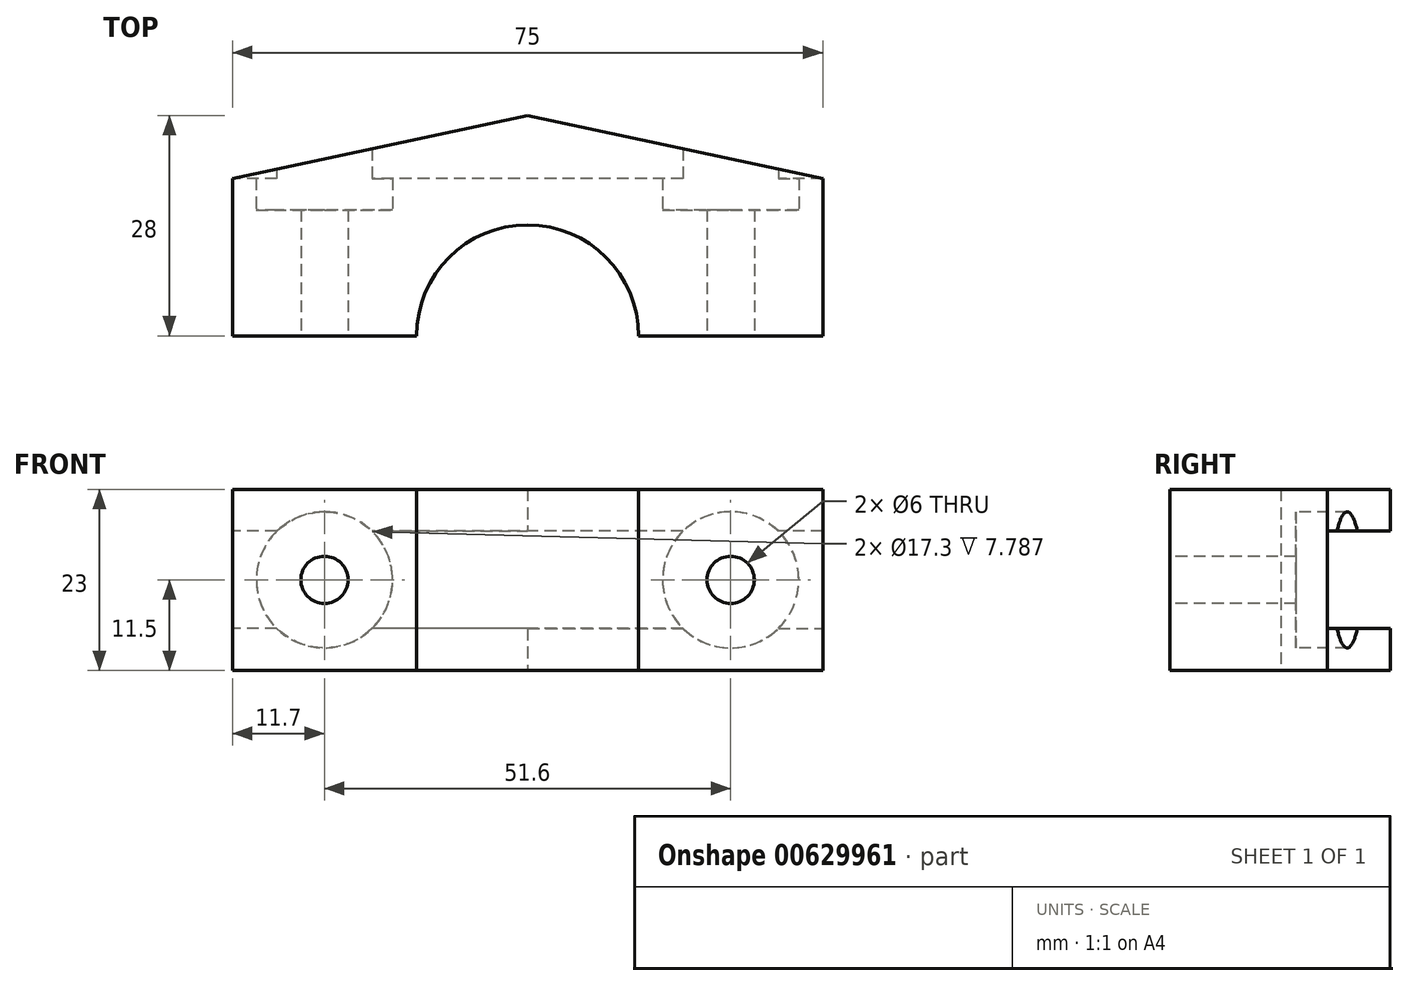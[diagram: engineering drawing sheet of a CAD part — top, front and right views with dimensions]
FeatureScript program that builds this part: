
annotation { "Feature Type Name" : "Feature", "Feature Type Description" : "" }
export const myFeature = defineFeature(function(context is Context, id is Id, definition is map)
    precondition{}
    {
        {
            var Q0;
            Q0=qCreatedBy(makeId("Top.planeOp"),FACE);
            var sketch = newSketch(context, id + "F0", { "sketchPlane" : qUnion([Q0])});
            skLineSegment(sketch, "E0.bottom", {"start": v(-37.5, 20) * mm, "end": v(37.5, 20) * mm});
            skLineSegment(sketch, "E0.top", {"start": v(-37.5, 0) * mm, "end": v(-14.1, 0) * mm});
            skLineSegment(sketch, "E0.left", {"start": v(-37.5, 20) * mm, "end": v(-37.5, 0) * mm});
            skLineSegment(sketch, "E0.right", {"start": v(37.5, 20) * mm, "end": v(37.5, 0) * mm});
            skLineSegment(sketch, "E1", {"start": v(14.1, 0) * mm, "end": v(37.5, 0) * mm});
            skArc(sketch, "E2", {"start": v(14.1, 0) * mm, "mid": v(0, 14.1) * mm, "end": v(-14.1, 0) * mm});
            skSolve(sketch);
        }
        {
            var Q0;
            Q0=makeQuery(id+"F0.imprint","IMPRINT",FACE,{"disambiguationData":[TD([[makeQuery(id+"F0.imprint","IMPRINT",EDGE,{"derivedFrom":sQuery(id+"F0.wireOp",EDGE,"E0.bottom")}),-1.0]])]});
            extrude(context, id + "F1", {"entities" : qUnion([Q0]), "depth" : 23 * mm, "offsetDistance" : 25 * mm});
        }
        {
            var Q0;
            Q0=makeQuery(id+"F1.opExtrude","SWEPT_FACE",FACE,{"disambiguationData":[OSD([sQuery(id+"F0.wireOp",EDGE,"E0.top")])]});
            var sketch = newSketch(context, id + "F2", { "sketchPlane" : qUnion([Q0])});
            skLineSegment(sketch, "E3", {"start": v(-14.1, 23) * mm, "end": v(-25.8, 11.5) * mm});
            skLineSegment(sketch, "E4", {"start": v(-37.5, 0) * mm, "end": v(-37.5, 23) * mm});
            skLineSegment(sketch, "E5", {"start": v(-37.5, 23) * mm, "end": v(-14.1, 0) * mm});
            skLineSegment(sketch, "E6", {"start": v(-25.8, 11.5) * mm, "end": v(-37.5, 0) * mm});
            skCircle(sketch, "E7", {"center": v(-25.8, 11.5) * mm, "radius": 3.02 * mm});
            skSolve(sketch);
        }
        {
            var Q0;
            Q0=makeQuery(id+"F1.opExtrude","SWEPT_FACE",FACE,{"disambiguationData":[OSD([sQuery(id+"F0.wireOp",EDGE,"E1")])]});
            var sketch = newSketch(context, id + "F3", { "sketchPlane" : qUnion([Q0])});
            skLineSegment(sketch, "E8", {"start": v(14.1, 23) * mm, "end": v(37.5, 0) * mm});
            skLineSegment(sketch, "E9", {"start": v(37.5, 0) * mm, "end": v(37.5, 23) * mm});
            skLineSegment(sketch, "E10", {"start": v(37.5, 23) * mm, "end": v(14.1, 0) * mm});
            skCircle(sketch, "E11", {"center": v(25.8, 11.5) * mm, "radius": 3 * mm});
            skSolve(sketch);
        }
        {
            var Q0;
            Q0=sQuery(id+"F2.wireOp",VERTEX,"E7.center");
            var Q1;
            Q1=makeQuery(id+"F1.opExtrude","SWEPT_BODY",BODY,{"disambiguationData":[OSD([sQuery(id+"F0.wireOp",EDGE,"E0.bottom"),sQuery(id+"F0.wireOp",EDGE,"E0.top"),sQuery(id+"F0.wireOp",EDGE,"E0.left"),sQuery(id+"F0.wireOp",EDGE,"E0.right"),sQuery(id+"F0.wireOp",EDGE,"E1"),sQuery(id+"F0.wireOp",EDGE,"E2")])]});
            hole(context, id + "F4", {"style" : HoleStyle.SIMPLE, "endStyle" : HoleEndStyle.THROUGH, "holeDiameter" : 6 * mm, "majorDiameter" : 5 * mm, "isTappedThrough" : true, "tappedDepth" : 12 * mm, "tapClearance" : 3, "locations" : qUnion([Q0]), "scope" : qUnion([Q1])});
        }
        {
            var Q0;
            Q0=sQuery(id+"F3.wireOp",VERTEX,"E11.center");
            var Q1;
            Q1=makeQuery(id+"F1.opExtrude","SWEPT_BODY",BODY,{"disambiguationData":[OSD([sQuery(id+"F0.wireOp",EDGE,"E0.bottom"),sQuery(id+"F0.wireOp",EDGE,"E0.top"),sQuery(id+"F0.wireOp",EDGE,"E0.left"),sQuery(id+"F0.wireOp",EDGE,"E0.right"),sQuery(id+"F0.wireOp",EDGE,"E1"),sQuery(id+"F0.wireOp",EDGE,"E2")])]});
            hole(context, id + "F5", {"style" : HoleStyle.SIMPLE, "endStyle" : HoleEndStyle.THROUGH, "holeDiameter" : 6 * mm, "majorDiameter" : 5 * mm, "isTappedThrough" : true, "tappedDepth" : 12 * mm, "tapClearance" : 3, "locations" : qUnion([Q0]), "scope" : qUnion([Q1])});
        }
        {
            var Q0;
            Q0=makeQuery(id+"F1.opExtrude","SWEPT_FACE",FACE,{"disambiguationData":[OSD([sQuery(id+"F0.wireOp",EDGE,"E0.bottom")])]});
            var sketch = newSketch(context, id + "F6", { "sketchPlane" : qUnion([Q0])});
            skLineSegment(sketch, "E12.bottom", {"start": v(-37.5, 23) * mm, "end": v(37.5, 23) * mm});
            skLineSegment(sketch, "E12.top", {"start": v(-37.5, 17.68) * mm, "end": v(-37.5, 17.68) * mm});
            skLineSegment(sketch, "E12.left", {"start": v(-37.5, 23) * mm, "end": v(-37.5, 17.68) * mm});
            skLineSegment(sketch, "E12.right", {"start": v(37.5, 23) * mm, "end": v(37.5, 17.68) * mm});
            skLineSegment(sketch, "E13.bottom", {"start": v(-37.5, 0) * mm, "end": v(37.5, 0) * mm});
            skLineSegment(sketch, "E13.top", {"start": v(-37.5, 5.32) * mm, "end": v(-37.5, 5.32) * mm});
            skLineSegment(sketch, "E13.left", {"start": v(-37.5, 0) * mm, "end": v(-37.5, 5.32) * mm});
            skLineSegment(sketch, "E13.right", {"start": v(37.5, 0) * mm, "end": v(37.5, 5.32) * mm});
            skLineSegment(sketch, "E14", {"start": v(-37.5, 17.68) * mm, "end": v(37.5, 17.68) * mm});
            skLineSegment(sketch, "E15", {"start": v(-37.5, 5.32) * mm, "end": v(37.5, 5.32) * mm});
            skSolve(sketch);
        }
        {
            var Q0;
            Q0 = qSketchRegion(id + "F6", true);
            extrude(context, id + "F7", {"entities" : qUnion([Q0]), "operationType" : NewBodyOperationType.ADD, "depth" : 8 * mm, "offsetDistance" : 25 * mm});
        }
        {
            var Q0;
            Q0=makeQuery(id+"F7.opExtrude","CAP_EDGE",EDGE,{"disambiguationData":[OSD([sQuery(id+"F6.wireOp",EDGE,"E13.left")])],"isStart":false});
            chamfer(context, id + "F8", {"entities" : qUnion([Q0]), "chamferType" : ChamferType.TWO_OFFSETS, "width1" : 37.5 * mm, "oppositeDirection" : false, "width2" : 8 * mm, "tangentPropagation" : true});
        }
        {
            var Q0;
            Q0=makeQuery(id+"F7.opExtrude","CAP_EDGE",EDGE,{"disambiguationData":[OSD([sQuery(id+"F6.wireOp",EDGE,"E12.left")])],"isStart":false});
            chamfer(context, id + "F9", {"entities" : qUnion([Q0]), "chamferType" : ChamferType.TWO_OFFSETS, "width1" : 37.5 * mm, "oppositeDirection" : false, "width2" : 8 * mm, "tangentPropagation" : true});
        }
        {
            var Q0;
            Q0=makeQuery(id+"F7.opExtrude","CAP_EDGE",EDGE,{"disambiguationData":[OSD([sQuery(id+"F6.wireOp",EDGE,"E12.right")])],"isStart":false});
            chamfer(context, id + "F10", {"entities" : qUnion([Q0]), "chamferType" : ChamferType.TWO_OFFSETS, "width1" : 8 * mm, "oppositeDirection" : false, "width2" : 37.5 * mm, "tangentPropagation" : true});
        }
        {
            var Q0;
            Q0=makeQuery(id+"F7.opExtrude","CAP_EDGE",EDGE,{"disambiguationData":[OSD([sQuery(id+"F6.wireOp",EDGE,"E13.right")])],"isStart":false});
            chamfer(context, id + "F11", {"entities" : qUnion([Q0]), "chamferType" : ChamferType.TWO_OFFSETS, "width1" : 8 * mm, "oppositeDirection" : false, "width2" : 37.5 * mm, "tangentPropagation" : true});
        }
        {
            var Q0;
            Q0=makeQuery(id+"F1.opExtrude","SWEPT_FACE",FACE,{"disambiguationData":[OSD([sQuery(id+"F0.wireOp",EDGE,"E0.bottom")])]});
            var sketch = newSketch(context, id + "F12", { "sketchPlane" : qUnion([Q0])});
            skCircle(sketch, "E16", {"center": v(25.8, 11.5) * mm, "radius": 8.65 * mm});
            skCircle(sketch, "E17", {"center": v(-25.8, 11.5) * mm, "radius": 8.65 * mm});
            skSolve(sketch);
        }
        {
            var Q0;
            Q0 = qSketchRegion(id + "F12", true);
            extrude(context, id + "F13", {"entities" : qUnion([Q0]), "operationType" : NewBodyOperationType.REMOVE, "endBound" : BoundingType.SYMMETRIC, "depth" : 8 * mm, "offsetDistance" : 25 * mm});
        }
    });
